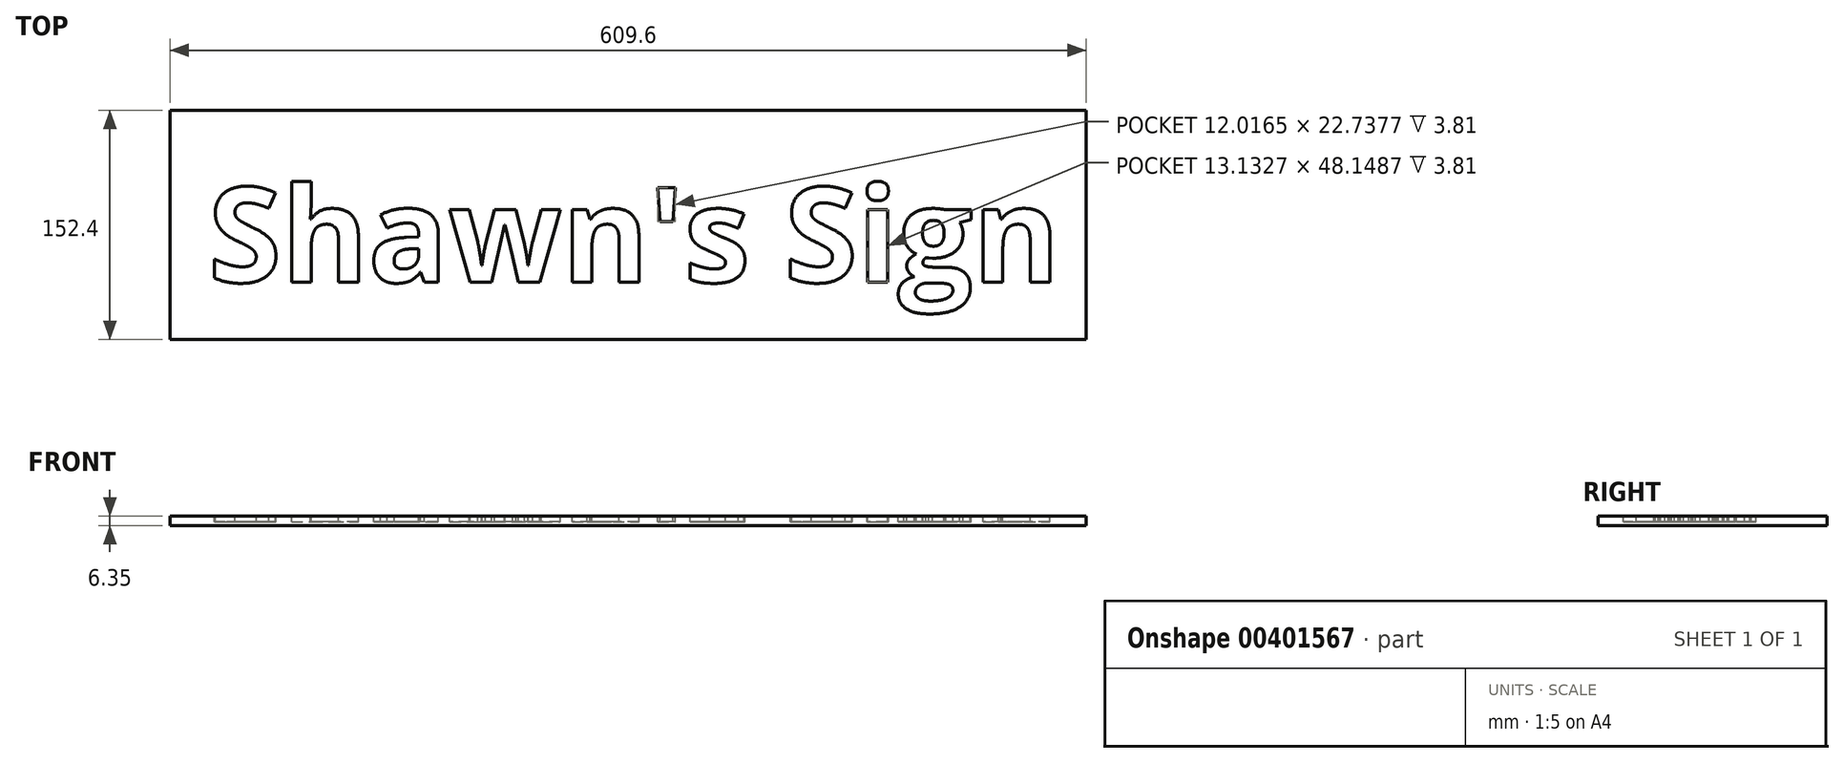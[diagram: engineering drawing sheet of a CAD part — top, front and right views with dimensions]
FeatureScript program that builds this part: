
annotation { "Feature Type Name" : "Feature", "Feature Type Description" : "" }
export const myFeature = defineFeature(function(context is Context, id is Id, definition is map)
    precondition{}
    {
        {
            var Q0;
            Q0=qCreatedBy(makeId("Top.planeOp"),FACE);
            var sketch = newSketch(context, id + "F0", { "sketchPlane" : qUnion([Q0])});
            skLineSegment(sketch, "E0.bottom", {"start": v(-116.22, -96.36) * mm, "end": v(493.38, -96.36) * mm});
            skLineSegment(sketch, "E0.top", {"start": v(-116.22, 56.04) * mm, "end": v(493.38, 56.04) * mm});
            skLineSegment(sketch, "E0.left", {"start": v(-116.22, -96.36) * mm, "end": v(-116.22, 56.04) * mm});
            skLineSegment(sketch, "E0.right", {"start": v(493.38, -96.36) * mm, "end": v(493.38, 56.04) * mm});
            skSolve(sketch);
        }
        {
            var Q0;
            Q0=makeQuery(id+"F0.imprint","IMPRINT",FACE,{"disambiguationData":[TD([[makeQuery(id+"F0.imprint","IMPRINT",EDGE,{"derivedFrom":sQuery(id+"F0.wireOp",EDGE,"E0.bottom")}),1.0]])]});
            extrude(context, id + "F1", {"entities" : qUnion([Q0]), "depth" : 6.35 * mm});
        }
        {
            var Q0;
            Q0=makeQuery(id+"F1.opExtrude","CAP_FACE",FACE,{"disambiguationData":[OSD([sQuery(id+"F0.wireOp",EDGE,"E0.bottom"),sQuery(id+"F0.wireOp",EDGE,"E0.top"),sQuery(id+"F0.wireOp",EDGE,"E0.left"),sQuery(id+"F0.wireOp",EDGE,"E0.right")])],"isStart":false});
            var sketch = newSketch(context, id + "F2", { "sketchPlane" : qUnion([Q0])});
            skText(sketch, "E1", { "text": "Shawn\'s Sign", "fontName": "OpenSans-Bold.ttf"});
            const initialGuessF2  = {"E1": [-0.09082, -0.05826, 1, 0, 0.0635]};
            skSetInitialGuess(sketch, initialGuessF2);
            skSolve(sketch);
        }
        {
            var Q0;
            Q0 = qSketchRegion(id + "F2", true);
            extrude(context, id + "F3", {"entities" : qUnion([Q0]), "operationType" : NewBodyOperationType.REMOVE, "oppositeDirection" : true, "depth" : 3.8 * mm});
        }
    });
